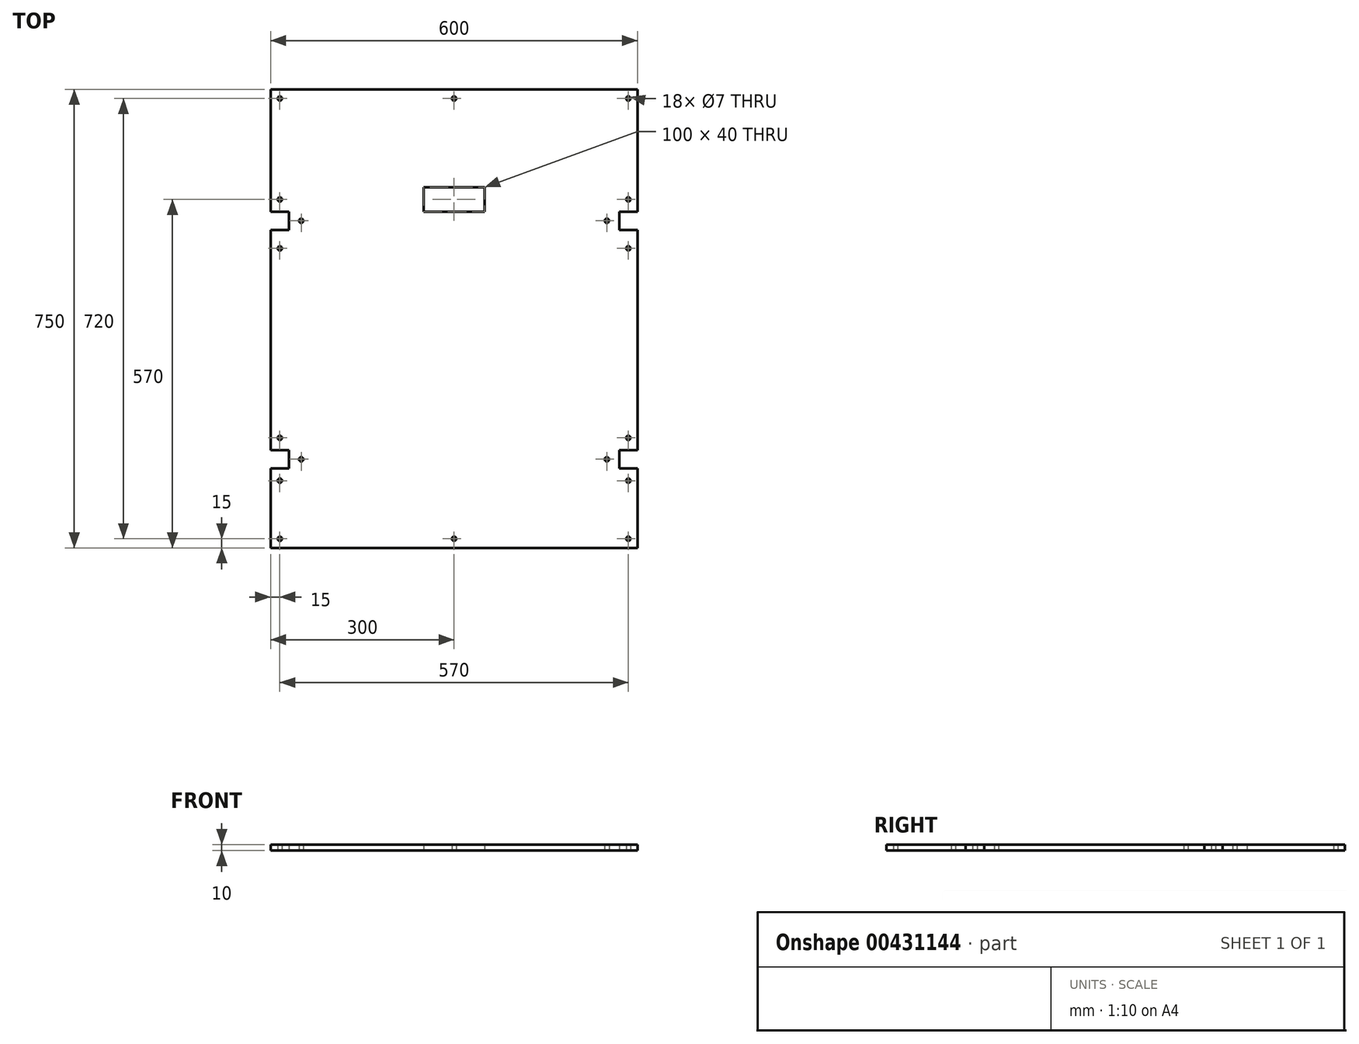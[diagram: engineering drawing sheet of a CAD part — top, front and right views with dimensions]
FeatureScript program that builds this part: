
annotation { "Feature Type Name" : "Feature", "Feature Type Description" : "" }
export const myFeature = defineFeature(function(context is Context, id is Id, definition is map)
    precondition{}
    {
        {
            var Q0;
            Q0=qCreatedBy(makeId("Top.planeOp"),FACE);
            var sketch = newSketch(context, id + "F0", { "sketchPlane" : qUnion([Q0])});
            skLineSegment(sketch, "E0.bottom", {"start": v(300, 375) * mm, "end": v(-300, 375) * mm});
            skLineSegment(sketch, "E0.top", {"start": v(300, -375) * mm, "end": v(-300, -375) * mm});
            skLineSegment(sketch, "E0.left", {"start": v(300, 375) * mm, "end": v(300, -375) * mm});
            skLineSegment(sketch, "E0.right", {"start": v(-300, 375) * mm, "end": v(-300, -375) * mm});
            skPoint(sketch, "E0.middle", {"position": v(0, 0) * mm});
            skLineSegment(sketch, "E1", {"start": v(0, 375) * mm, "end": v(0, -375) * mm, "construction": true});
            skLineSegment(sketch, "E2", {"start": v(-285, 375) * mm, "end": v(-285, -375) * mm, "construction": true});
            skLineSegment(sketch, "E3.bottom", {"start": v(-300, 175) * mm, "end": v(-270, 175) * mm});
            skLineSegment(sketch, "E3.top", {"start": v(-300, 145) * mm, "end": v(-270, 145) * mm});
            skLineSegment(sketch, "E3.left", {"start": v(-300, 175) * mm, "end": v(-300, 145) * mm});
            skLineSegment(sketch, "E3.right", {"start": v(-270, 175) * mm, "end": v(-270, 145) * mm});
            skLineSegment(sketch, "E4.bottom", {"start": v(-300, -215) * mm, "end": v(-270, -215) * mm});
            skLineSegment(sketch, "E4.top", {"start": v(-300, -245) * mm, "end": v(-270, -245) * mm});
            skLineSegment(sketch, "E4.left", {"start": v(-300, -215) * mm, "end": v(-300, -245) * mm});
            skLineSegment(sketch, "E4.right", {"start": v(-270, -215) * mm, "end": v(-270, -245) * mm});
            skLineSegment(sketch, "E5.bottom", {"start": v(-50, 175) * mm, "end": v(50, 175) * mm});
            skLineSegment(sketch, "E5.top", {"start": v(-50, 215) * mm, "end": v(50, 215) * mm});
            skLineSegment(sketch, "E5.left", {"start": v(-50, 175) * mm, "end": v(-50, 215) * mm});
            skLineSegment(sketch, "E5.right", {"start": v(50, 175) * mm, "end": v(50, 215) * mm});
            skCircle(sketch, "E6", {"center": v(-285, 360) * mm, "radius": 3.5 * mm});
            skCircle(sketch, "E7", {"center": v(-285, 195) * mm, "radius": 3.5 * mm});
            skCircle(sketch, "E8", {"center": v(-250, 160) * mm, "radius": 3.5 * mm});
            skPoint(sketch, "E8.centerSnap0", {"position": v(-270, 160) * mm});
            skCircle(sketch, "E9", {"center": v(-285, 115) * mm, "radius": 3.5 * mm});
            skCircle(sketch, "E10", {"center": v(-285, -195) * mm, "radius": 3.5 * mm});
            skCircle(sketch, "E11", {"center": v(-250, -230) * mm, "radius": 3.5 * mm});
            skPoint(sketch, "E11.centerSnap0", {"position": v(-270, -230) * mm});
            skCircle(sketch, "E12", {"center": v(-285, -265) * mm, "radius": 3.5 * mm});
            skCircle(sketch, "E13", {"center": v(-285, -360) * mm, "radius": 3.5 * mm});
            skCircle(sketch, "E14.MirrorC", {"center": v(285, 360) * mm, "radius": 3.5 * mm});
            skCircle(sketch, "E15.MirrorC", {"center": v(285, 195) * mm, "radius": 3.5 * mm});
            skLineSegment(sketch, "E16.MirrorCS", {"start": v(270, 175) * mm, "end": v(270, 145) * mm});
            skCircle(sketch, "E17.MirrorC", {"center": v(250, 160) * mm, "radius": 3.5 * mm});
            skLineSegment(sketch, "E18.MirrorCS", {"start": v(300, 145) * mm, "end": v(270, 145) * mm});
            skCircle(sketch, "E19.MirrorC", {"center": v(285, 115) * mm, "radius": 3.5 * mm});
            skCircle(sketch, "E20.MirrorC", {"center": v(285, -195) * mm, "radius": 3.5 * mm});
            skLineSegment(sketch, "E21.MirrorCS", {"start": v(300, -215) * mm, "end": v(270, -215) * mm});
            skLineSegment(sketch, "E22.MirrorCS", {"start": v(300, -245) * mm, "end": v(270, -245) * mm});
            skCircle(sketch, "E23.MirrorC", {"center": v(285, -265) * mm, "radius": 3.5 * mm});
            skLineSegment(sketch, "E24.MirrorCS", {"start": v(270, -215) * mm, "end": v(270, -245) * mm});
            skCircle(sketch, "E25.MirrorC", {"center": v(250, -230) * mm, "radius": 3.5 * mm});
            skCircle(sketch, "E26.MirrorC", {"center": v(285, -360) * mm, "radius": 3.5 * mm});
            skCircle(sketch, "E27", {"center": v(0, 360) * mm, "radius": 3.5 * mm});
            skLineSegment(sketch, "E28.MirrorCS", {"start": v(300, 175) * mm, "end": v(270, 175) * mm});
            skCircle(sketch, "E29", {"center": v(0, -360) * mm, "radius": 3.5 * mm});
            skSolve(sketch);
        }
        {
            var Q0;
            {var subQ5=sQuery(id+"F0.wireOp",EDGE,"E0.bottom");Q0=makeQuery(id+"F0.imprint","IMPRINT",FACE,{"disambiguationData":[TD([[makeQuery(id+"F0.imprint","IMPRINT",EDGE,{"derivedFrom":subQ5}),1.0]])]});}
            extrude(context, id + "F1", {"entities" : qUnion([Q0]), "depth" : 10 * mm, "offsetDistance" : 25 * mm});
        }
    });
